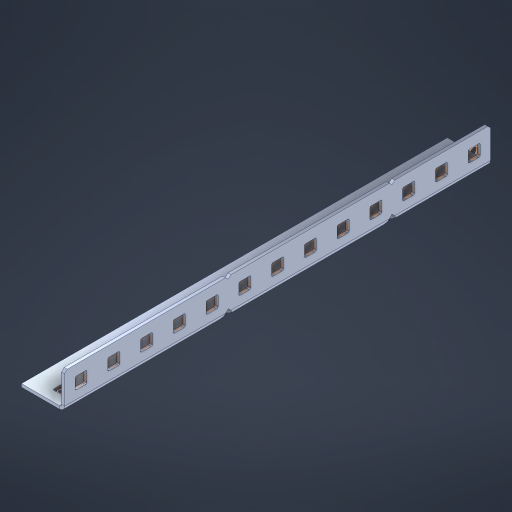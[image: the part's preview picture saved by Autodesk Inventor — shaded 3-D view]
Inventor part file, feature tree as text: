
AUTODESK INVENTOR PART (.ipt)
format: ipt  version: 2023 (Build 270158000, 158)  size: 619,008 bytes
history: native  units: in
note: dims shown in document units (in); Inventor stores cm internally (conversion verified against a paired STEP export)
features: other x31, extrude x25, sheet_metal_op x10, sketch x8, mirror x1, pattern_linear x1, chamfer x1
ambient origin geometry x8: Origin, YZ Plane, XZ Plane, XY Plane, X Axis, Y Axis, Z Axis, Center Point
bodies: Solid1 (feature_tree), Body (feature_tree)
feature tree (77):
  other  "Flange Pattern Plane"
  sheet_metal_op  "Flange Pattern"
  sheet_metal_op  "Body Pattern"
  other  "Arc Length"
  mirror  "Notch Mirror"
  pattern_linear  "Notch Pattern"  Spacing1=0.1875in  [1 undecoded]
  chamfer  "End Chamfer"
  extrude  "Half Cut"  Depth=0.0469in
  sketch  "Sketch1"  dims[d0=2.5in]
  other  "Plate1"
  sketch  "Sketch2"  dims[d1=6.5in]
  other  "Plate2"
  sheet_metal_op  "Bend1"
  sheet_metal_op  "Corner1"
  sketch  "Sketch3"  dims[d2=0.0469in]
  other  "Flange Pattern Sketch"
  sketch  "Sketch7"  dims[d3=0.0469in]
  other  "Srf1"
  other  "Srf2"
  sketch  "Sketch8"  dims[d4=0.0234in]
  sketch  "Sketch9"  dims[d5=0.0938in]
  other  "Srf91"
  sheet_metal_op  "Body Pattern Sketch"
  other  "Srf92"
  sketch  "Sketch13"  dims[d6=0.0469in]
  sketch  "Sketch14"  dims[d7=0.5in d8=90.0deg d9=0.0312in d10=0.1875in d11=0.0469in d12=0.0469in d16=0.182in d17=0.02in d18=0.0469in d19=0.0in d20=0.25in d21=0.25in d46=0.172in d47=1.0in d48=0.0in d49=0.182in d50=0.02in d51=0.25in d52=0.25in d53=0.0469in d54=0.0in d55=0.172in d56=1.0in d57=0.0in d60=5.1181in d62=0.5in d63=0.3937in d65=0.5in d85=0.1227in d86=0.1659in d88=0.04in d89=0.0469in d90=0.0in d91=0.04in d92=0.0491in d95=2.5in d96=0.04in d97=0.25in d98=45.0deg d101=0.0in d102=2.497in d131=0.5in d132=5.1181in d134=0.5in d139=0.5in]
  other  "Srf856"
  other  "Srf1310"
  other  "Srf1311"
  other  "Srf1312"
  other  "Srf1376"
  other  "Srf1377"
  other  "Srf1728"
  other  "Srf1755"
  other  "Srf1878"
  other  "Srf1879"
  other  "Srf1880"
  other  "Srf1881"
  other  "Srf1882"
  other  "Srf1883"
  other  "Srf1884"
  other  "Srf1942"
  other  "Srf1943"
  other  "Srf1944"
  other  "Srf1945"
  other  "Srf1946"
  other  "Srf1947"
  other  "Srf1948"
  sheet_metal_op  "Flange Stamp"
  sheet_metal_op  "Flange Circle"
  sheet_metal_op  "Body Stamp"
  sheet_metal_op  "Body Circle"
  sheet_metal_op  "Notch"
  extrude  "ExtrusionSrf2"  Depth=0.0469in
  extrude  "ExtrusionSrf92"  Depth=0.5in
  extrude  "ExtrusionSrf856"  Depth=0.02in
  extrude  "ExtrusionSrf1310"  Depth=0.0469in
  extrude  "ExtrusionSrf1311"  TaperAngle=0.0deg  [1 undecoded]
  extrude  "ExtrusionSrf1312"  Depth=0.5in
  extrude  "ExtrusionSrf1376"  Depth=0.5in
  extrude  "ExtrusionSrf1377"  Depth=0.5in
  extrude  "ExtrusionSrf1728"  Depth=0.5in TaperAngle=0.0deg
  extrude  "ExtrusionSrf1755"  Depth=0.5in
  extrude  "ExtrusionSrf1878"  Depth=0.02in
  extrude  "ExtrusionSrf1879"  Depth=0.5in
  extrude  "ExtrusionSrf1880"  Depth=0.5in
  extrude  "ExtrusionSrf1881"  Depth=0.0469in
  extrude  "ExtrusionSrf1882"  TaperAngle=0.0deg  [1 undecoded]
  extrude  "ExtrusionSrf1883"  Depth=0.5in
  extrude  "ExtrusionSrf1884"  Depth=0.5in TaperAngle=0.0deg
  extrude  "ExtrusionSrf1942"  Depth=0.5in
  extrude  "ExtrusionSrf1943"  Depth=0.5in
  extrude  "ExtrusionSrf1944"  Depth=0.5in
  extrude  "ExtrusionSrf1945"  Depth=0.5in
  extrude  "ExtrusionSrf1946"  Depth=0.5in
  extrude  "ExtrusionSrf1947"  Depth=0.0469in
  extrude  "ExtrusionSrf1948"  TaperAngle=0.0deg  [1 undecoded]
note: 4 required parameter values undecoded (feature->parameter linkage not recoverable at this tier; creation-order binding heuristic only, values carry confidence <= 0.55)
